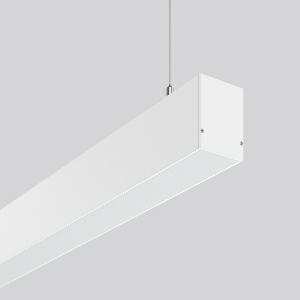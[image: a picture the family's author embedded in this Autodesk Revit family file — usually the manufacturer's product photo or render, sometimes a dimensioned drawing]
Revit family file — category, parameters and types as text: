
# Revit family: less_is_more_50_312312_002_c555
name_source: partatom
category: Lighting Fixtures
units: mm (PartAtom-declared; Revit-internal decimal feet)

## family parameters
Cut with Voids When Loaded = No
Host = Face
Light Source = No
Part Type = Normal
Room Calculation Point = No
Round Connector Dimension = Use Diameter
Shared = No

## types (1)
- LESS IS MORE 50 (1 x LED Modul 830, 3100 lm, 3000)
    Apparent Load = 28 VA
    CIE Flux Codes = 48 79 95 100 100
    Color Rendering = 80
    Color Temperature = 3000
    Default Elevation = 1800 mm
    Description = Series: LESS IS MORE 50
Linear pendant luminaire for aesthetically sophisticated lighting. Housing: extruded aluminium profile, powder-coated. End cap aluminium powder-coated. Canopy made of aluminium, powder-coated. Diffuser made of non-yellowing plastic (PMMA), opal. Direct light emission. Suitable for pendant. 2-point steel cable suspension freely positionable and infinitely height-adjustable. Special lengths available on request. LED unit with integrated converter interchangeable and removable. Suitable for through-wiring. With sensors or as a safety luminaire on request. 
Colour: traffic white, matt (RAL 9016)
Length: 1127 mm
Width: 57 mm
Height: 75 mm
Suspension length: 2000 mm
Lamp: LED
Socket: without socket
Colour temperature: 3000K
Colour rendering index (CRI): 80
System power: 28 W
Rated luminous flux: 3100 lm
Luminous efficiency: 111 lm/W
Control gear: Regulated power supply
Protection class: I
Type of protection: IP 20
    Height = 75 mm
    Lamp = 1 x LED Modul 830
    Lamp Light Flux = 3100 lm
    Lamp count = 1
    Length = 1127 mm
    Lifetime = 50000 h
    Luminous efficacy = 111 lm/W
    Manufacturer = RZB
    ModVariant = No
    Model = 312312.002
    Mounting Place = Ceiling
    Mounting Type = Pendant
    Number of Poles = 1
    OnlyDefault = Yes
    Power Factor = 1
    Product Name = LESS IS MORE 50
    Product group = Pendant LED linear luminaires
    ProductGroupID = 907
    Protection Class = Protection class I
    Protection Degree = IP 20
    RLX_Detail_Level = 1
    RLX_Emergency_Light_Flux = 0 lm
    RLX_Emergency_Type = 0
    RLX_Emergency_Type_DB = No
    RlxData = <blob elided: 20637 chars, md5=6401afc4>
    Socket = socket
    Standby Power = 0 W
    System Light Flux = 3100 lm
    System Power = 28 W
    Type Comments = Product without accessories
    Type Image = 312318.002.jpg
    URL = http://relux.com
    VarID = ---
    Voltage = 230 V
    Voltage Range = 220-240 V
    Weight = 0.00 kg
    Width = 57 mm

## geometry (parser evidence)
native form markers: Blend x4, Sweep x10
no freeform markers — native parametric forms only
